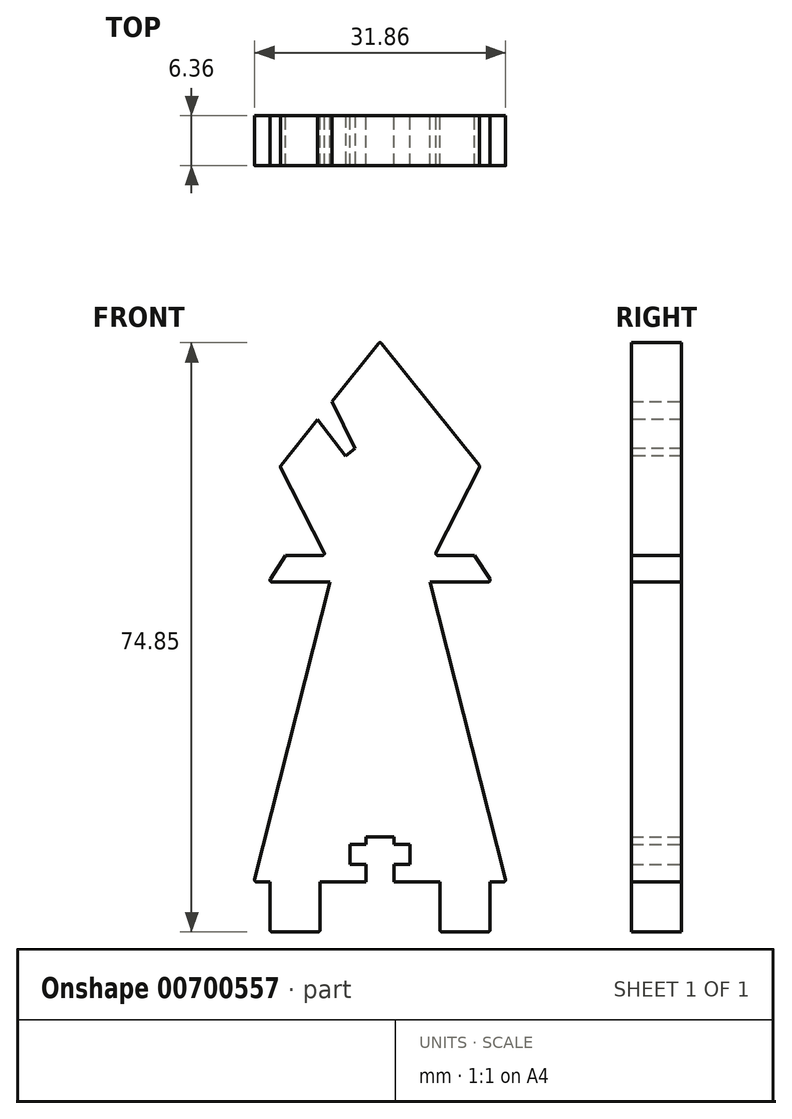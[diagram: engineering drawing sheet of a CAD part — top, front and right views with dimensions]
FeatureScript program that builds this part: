
annotation { "Feature Type Name" : "Feature", "Feature Type Description" : "" }
export const myFeature = defineFeature(function(context is Context, id is Id, definition is map)
    precondition{}
    {
        {
            var Q0;
            Q0=qCreatedBy(makeId("Front.planeOp"),FACE);
            var sketch = newSketch(context, id + "F0", { "sketchPlane" : qUnion([Q0])});
            skLineSegment(sketch, "E0", {"start": v(0, 0) * mm, "end": v(-7.62, 0) * mm});
            skLineSegment(sketch, "E1", {"start": v(0, 0) * mm, "end": v(0, 38.1) * mm});
            skLineSegment(sketch, "E2", {"start": v(0, 38.1) * mm, "end": v(0, 38.1) * mm});
            skLineSegment(sketch, "E3", {"start": v(0, 38.1) * mm, "end": v(-6.35, 38.1) * mm});
            skPoint(sketch, "E3.endSnap0", {"position": v(-8, 0) * mm});
            skLineSegment(sketch, "E4", {"start": v(-13.97, 0) * mm, "end": v(-15.68, 0) * mm, "construction": true});
            skLineSegment(sketch, "E5", {"start": v(-6.35, 38.1) * mm, "end": v(-12, 38.1) * mm});
            skPoint(sketch, "E5.endSnap0", {"position": v(-12, 0) * mm});
            skLineSegment(sketch, "E6", {"start": v(-12, 38.1) * mm, "end": v(-12, 41.48) * mm});
            skLineSegment(sketch, "E7", {"start": v(-7.34, 41.48) * mm, "end": v(-12, 41.48) * mm});
            skPoint(sketch, "E8.start.orphan", {"position": v(-12, 38.1) * mm});
            skLineSegment(sketch, "E9.MirrorCS", {"start": v(0, 0) * mm, "end": v(7.62, 0) * mm});
            skLineSegment(sketch, "E10.MirrorCS", {"start": v(13.97, 0) * mm, "end": v(15.68, 0) * mm, "construction": true});
            skLineSegment(sketch, "E11.MirrorCS", {"start": v(0, 38.1) * mm, "end": v(6.35, 38.1) * mm});
            skLineSegment(sketch, "E12.MirrorCS", {"start": v(6.35, 38.1) * mm, "end": v(12, 38.1) * mm});
            skLineSegment(sketch, "E13.MirrorCS", {"start": v(12, 38.1) * mm, "end": v(12, 41.48) * mm});
            skLineSegment(sketch, "E14.MirrorCS", {"start": v(7.34, 41.48) * mm, "end": v(12, 41.48) * mm});
            skPoint(sketch, "E15.MirrorP", {"position": v(8, 0) * mm});
            skPoint(sketch, "E16.MirrorP", {"position": v(12, 38.1) * mm});
            skPoint(sketch, "E17.MirrorP", {"position": v(12, 0) * mm});
            skLineSegment(sketch, "E18", {"start": v(0, 38.1) * mm, "end": v(0, 57.15) * mm, "construction": true});
            skLineSegment(sketch, "E19.top", {"start": v(-7.87, -6.35) * mm, "end": v(-13.72, -6.35) * mm});
            skLineSegment(sketch, "E19.left", {"start": v(-7.62, 0) * mm, "end": v(-7.62, -6.1) * mm});
            skLineSegment(sketch, "E19.right", {"start": v(-13.97, 0) * mm, "end": v(-13.97, -6.1) * mm});
            skLineSegment(sketch, "E20.MirrorCS", {"start": v(7.87, -6.35) * mm, "end": v(13.72, -6.35) * mm});
            skLineSegment(sketch, "E21.MirrorCS", {"start": v(13.97, 0) * mm, "end": v(13.97, -6.1) * mm});
            skLineSegment(sketch, "E22.MirrorCS", {"start": v(7.62, 0) * mm, "end": v(7.62, -6.1) * mm});
            skLineSegment(sketch, "E23.trimOffspring", {"start": v(-13.97, 0) * mm, "end": v(-16, 0) * mm});
            skLineSegment(sketch, "E24.trimOffspring", {"start": v(13.97, 0) * mm, "end": v(16, 0) * mm});
            skLineSegment(sketch, "E25", {"start": v(-7.11, 41.85) * mm, "end": v(-12.63, 52.65) * mm});
            skLineSegment(sketch, "E26", {"start": v(-12.6, 52.92) * mm, "end": v(-0.2, 68.4) * mm});
            skLineSegment(sketch, "E27", {"start": v(0.2, 68.4) * mm, "end": v(12.6, 52.92) * mm});
            skLineSegment(sketch, "E28", {"start": v(12.63, 52.65) * mm, "end": v(7.11, 41.85) * mm});
            skLineSegment(sketch, "E29", {"start": v(-6.35, 38.1) * mm, "end": v(-15.92, 0.32) * mm});
            skLineSegment(sketch, "E30", {"start": v(6.35, 38.1) * mm, "end": v(15.92, 0.32) * mm});
            skLineSegment(sketch, "E31", {"start": v(-12, 38.1) * mm, "end": v(-13.72, 38.1) * mm});
            skLineSegment(sketch, "E32", {"start": v(-13.93, 38.5) * mm, "end": v(-12, 41.48) * mm});
            skLineSegment(sketch, "E33", {"start": v(12, 38.1) * mm, "end": v(13.72, 38.1) * mm});
            skLineSegment(sketch, "E34", {"start": v(13.93, 38.5) * mm, "end": v(12, 41.48) * mm});
            skPoint(sketch, "E35.visualSharp", {"position": v(0, 68.66) * mm});
            skArc(sketch, "E35.filletArc", {"start": v(0.2, 68.4) * mm, "mid": v(0, 68.5) * mm, "end": v(-0.2, 68.4) * mm});
            skPoint(sketch, "E36.visualSharp", {"position": v(-14.19, 38.1) * mm});
            skArc(sketch, "E36.filletArc", {"start": v(-13.93, 38.5) * mm, "mid": v(-13.94, 38.23) * mm, "end": v(-13.72, 38.1) * mm});
            skPoint(sketch, "E37.visualSharp", {"position": v(14.19, 38.1) * mm});
            skArc(sketch, "E37.filletArc", {"start": v(13.72, 38.1) * mm, "mid": v(13.94, 38.23) * mm, "end": v(13.93, 38.5) * mm});
            skPoint(sketch, "E38.visualSharp", {"position": v(-12.7, 52.8) * mm});
            skArc(sketch, "E38.filletArc", {"start": v(-12.6, 52.92) * mm, "mid": v(-12.65, 52.79) * mm, "end": v(-12.63, 52.65) * mm});
            skPoint(sketch, "E39.visualSharp", {"position": v(12.7, 52.8) * mm});
            skArc(sketch, "E39.filletArc", {"start": v(12.63, 52.65) * mm, "mid": v(12.65, 52.79) * mm, "end": v(12.6, 52.92) * mm});
            skPoint(sketch, "E40.newPointA", {"position": v(6.92, 41.48) * mm});
            skPoint(sketch, "E40.newPointB", {"position": v(0, 41.48) * mm});
            skArc(sketch, "E40.filletArc", {"start": v(7.11, 41.85) * mm, "mid": v(7.12, 41.6) * mm, "end": v(7.34, 41.48) * mm});
            skPoint(sketch, "E41.newPointA", {"position": v(-6.92, 41.48) * mm});
            skArc(sketch, "E41.filletArc", {"start": v(-7.34, 41.48) * mm, "mid": v(-7.12, 41.6) * mm, "end": v(-7.11, 41.85) * mm});
            skPoint(sketch, "E42.visualSharp", {"position": v(-16, 0) * mm});
            skArc(sketch, "E42.filletArc", {"start": v(-15.92, 0.32) * mm, "mid": v(-15.88, 0.1) * mm, "end": v(-15.68, 0) * mm});
            skPoint(sketch, "E43.visualSharp", {"position": v(16, 0) * mm});
            skArc(sketch, "E43.filletArc", {"start": v(15.68, 0) * mm, "mid": v(15.88, 0.1) * mm, "end": v(15.92, 0.32) * mm});
            skPoint(sketch, "E44.visualSharp", {"position": v(-13.97, -6.35) * mm});
            skArc(sketch, "E44.filletArc", {"start": v(-13.97, -6.1) * mm, "mid": v(-13.9, -6.28) * mm, "end": v(-13.72, -6.35) * mm});
            skPoint(sketch, "E45.visualSharp", {"position": v(-7.62, -6.35) * mm});
            skArc(sketch, "E45.filletArc", {"start": v(-7.87, -6.35) * mm, "mid": v(-7.7, -6.28) * mm, "end": v(-7.62, -6.1) * mm});
            skPoint(sketch, "E46.visualSharp", {"position": v(7.62, -6.35) * mm});
            skArc(sketch, "E46.filletArc", {"start": v(7.62, -6.1) * mm, "mid": v(7.7, -6.28) * mm, "end": v(7.87, -6.35) * mm});
            skPoint(sketch, "E47.visualSharp", {"position": v(13.97, -6.35) * mm});
            skArc(sketch, "E47.filletArc", {"start": v(13.72, -6.35) * mm, "mid": v(13.9, -6.28) * mm, "end": v(13.97, -6.1) * mm});
            skSolve(sketch);
        }
        {
            var Q0;
            Q0 = qSketchRegion(id + "F0", true);
            extrude(context, id + "F1", {"entities" : qUnion([Q0]), "depth" : 3.17 * mm, "offsetDistance" : 25.4 * mm, "hasSecondDirection" : true, "secondDirectionOppositeDirection" : true, "secondDirectionDepth" : 3.17 * mm});
        }
        {
            var Q0;
            Q0=qCreatedBy(makeId("Front.planeOp"),FACE);
            var sketch = newSketch(context, id + "F2", { "sketchPlane" : qUnion([Q0])});
            skLineSegment(sketch, "E48", {"start": v(-7.73, 64.25) * mm, "end": v(-9.85, 61.3) * mm});
            skLineSegment(sketch, "E49", {"start": v(-9.85, 61.3) * mm, "end": v(-4.41, 54.11) * mm});
            skLineSegment(sketch, "E50", {"start": v(-4.41, 54.11) * mm, "end": v(-3.16, 55.06) * mm});
            skLineSegment(sketch, "E51", {"start": v(-3.16, 55.06) * mm, "end": v(-7.73, 64.25) * mm});
            skSolve(sketch);
        }
        {
            var Q0;
            Q0 = qSketchRegion(id + "F2", true);
            extrude(context, id + "F3", {"entities" : qUnion([Q0]), "operationType" : NewBodyOperationType.REMOVE, "oppositeDirection" : true, "depth" : 25.4 * mm, "offsetDistance" : 25.4 * mm, "hasSecondDirection" : true, "secondDirectionOppositeDirection" : false, "secondDirectionDepth" : 25.4 * mm});
        }
        {
            var Q0;
            Q0=qCreatedBy(makeId("Front.planeOp"),FACE);
            var sketch = newSketch(context, id + "F4", { "sketchPlane" : qUnion([Q0])});
            skLineSegment(sketch, "E52", {"start": v(-50.6, 17.32) * mm, "end": v(-50.6, 17.32) * mm});
            skLineSegment(sketch, "E53.bottom", {"start": v(-1.78, 5.72) * mm, "end": v(1.78, 5.72) * mm});
            skLineSegment(sketch, "E53.left", {"start": v(-1.78, 5.72) * mm, "end": v(-1.78, 4.76) * mm});
            skLineSegment(sketch, "E54", {"start": v(0, 5.71) * mm, "end": v(0, 9.6) * mm, "construction": true});
            skLineSegment(sketch, "E55.bottom", {"start": v(-1.78, 4.76) * mm, "end": v(-3.81, 4.76) * mm});
            skLineSegment(sketch, "E55.top", {"start": v(-1.78, 2.22) * mm, "end": v(-3.81, 2.22) * mm});
            skLineSegment(sketch, "E55.right", {"start": v(-3.81, 4.76) * mm, "end": v(-3.81, 2.22) * mm});
            skLineSegment(sketch, "E56.top", {"start": v(-1.78, 0) * mm, "end": v(1.78, 0) * mm});
            skLineSegment(sketch, "E56.left", {"start": v(-1.78, 2.22) * mm, "end": v(-1.78, 0) * mm});
            skLineSegment(sketch, "E57.MirrorCS", {"start": v(0, 5.72) * mm, "end": v(0, 9.6) * mm, "construction": true});
            skLineSegment(sketch, "E58.MirrorCS", {"start": v(3.8, 4.76) * mm, "end": v(3.8, 2.22) * mm});
            skLineSegment(sketch, "E59.MirrorCS", {"start": v(1.78, 5.72) * mm, "end": v(1.78, 4.76) * mm});
            skLineSegment(sketch, "E60.MirrorCS", {"start": v(1.78, 2.22) * mm, "end": v(1.78, 0) * mm});
            skLineSegment(sketch, "E61.MirrorCS", {"start": v(1.78, 4.76) * mm, "end": v(3.8, 4.76) * mm});
            skLineSegment(sketch, "E62.MirrorCS", {"start": v(1.78, 0) * mm, "end": v(-1.78, 0) * mm});
            skLineSegment(sketch, "E63.MirrorCS", {"start": v(1.78, 2.22) * mm, "end": v(3.8, 2.22) * mm});
            skLineSegment(sketch, "E64.MirrorCS", {"start": v(1.78, 5.72) * mm, "end": v(-1.78, 5.72) * mm});
            skSolve(sketch);
        }
        {
            var Q0;
            Q0 = qSketchRegion(id + "F4", true);
            extrude(context, id + "F5", {"entities" : qUnion([Q0]), "operationType" : NewBodyOperationType.REMOVE, "depth" : 25.4 * mm, "offsetDistance" : 25.4 * mm, "hasSecondDirection" : true, "secondDirectionOppositeDirection" : true, "secondDirectionDepth" : 25.4 * mm});
        }
    });
